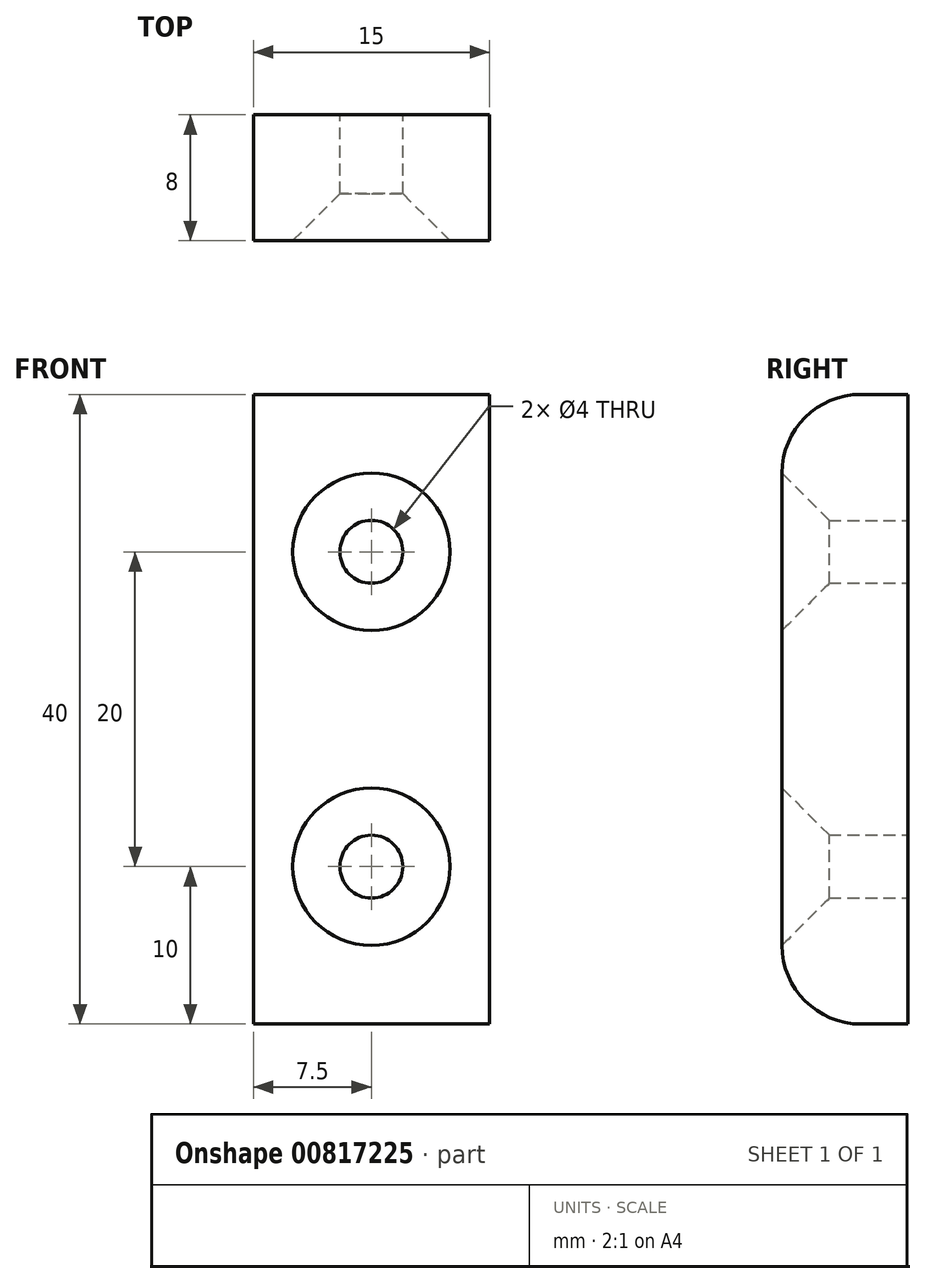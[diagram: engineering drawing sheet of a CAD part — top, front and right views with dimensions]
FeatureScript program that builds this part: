
annotation { "Feature Type Name" : "Feature", "Feature Type Description" : "" }
export const myFeature = defineFeature(function(context is Context, id is Id, definition is map)
    precondition{}
    {
        {
            var Q0;
            Q0=qCreatedBy(makeId("Front.planeOp"),FACE);
            var sketch = newSketch(context, id + "F0", { "sketchPlane" : qUnion([Q0])});
            skLineSegment(sketch, "E0", {"start": v(0, 0) * mm, "end": v(0, -20) * mm});
            skLineSegment(sketch, "E1", {"start": v(0, -20) * mm, "end": v(15, -20) * mm});
            skLineSegment(sketch, "E2", {"start": v(15, -20) * mm, "end": v(15, 0) * mm});
            skCircle(sketch, "E3", {"center": v(7.5, -10) * mm, "radius": 2 * mm});
            skCircle(sketch, "E4.MirrorC", {"center": v(7.5, 10) * mm, "radius": 2 * mm});
            skLineSegment(sketch, "E5.MirrorCS", {"start": v(0, 0) * mm, "end": v(0, 20) * mm});
            skLineSegment(sketch, "E6.MirrorCS", {"start": v(0, 20) * mm, "end": v(15, 20) * mm});
            skLineSegment(sketch, "E7.MirrorCS", {"start": v(15, 20) * mm, "end": v(15, 0) * mm});
            skSolve(sketch);
        }
        {
            var Q0;
            Q0 = qSketchRegion(id + "F0", true);
            extrude(context, id + "F1", {"entities" : qUnion([Q0]), "depth" : 8 * mm, "offsetDistance" : 25 * mm});
        }
        {
            var Q0;
            Q0=makeQuery(id+"F1.opExtrude","CAP_EDGE",EDGE,{"disambiguationData":[OSD([sQuery(id+"F0.wireOp",EDGE,"E4.MirrorC")])],"isStart":false});
            var Q1;
            Q1=makeQuery(id+"F1.opExtrude","CAP_EDGE",EDGE,{"disambiguationData":[OSD([sQuery(id+"F0.wireOp",EDGE,"E3")])],"isStart":false});
            chamfer(context, id + "F2", {"entities" : qUnion([Q0, Q1]), "width" : 3 * mm, "tangentPropagation" : true});
        }
        {
            var Q0;
            Q0=makeQuery(id+"F1.opExtrude","CAP_EDGE",EDGE,{"disambiguationData":[OSD([sQuery(id+"F0.wireOp",EDGE,"E6.MirrorCS")])],"isStart":false});
            var Q1;
            Q1=makeQuery(id+"F1.opExtrude","CAP_EDGE",EDGE,{"disambiguationData":[OSD([sQuery(id+"F0.wireOp",EDGE,"E1")])],"isStart":false});
            fillet(context, id + "F3", {"entities" : qUnion([Q0, Q1]), "radius" : 5 * mm, "tangentPropagation" : true, "allowEdgeOverflow" : false});
        }
    });
